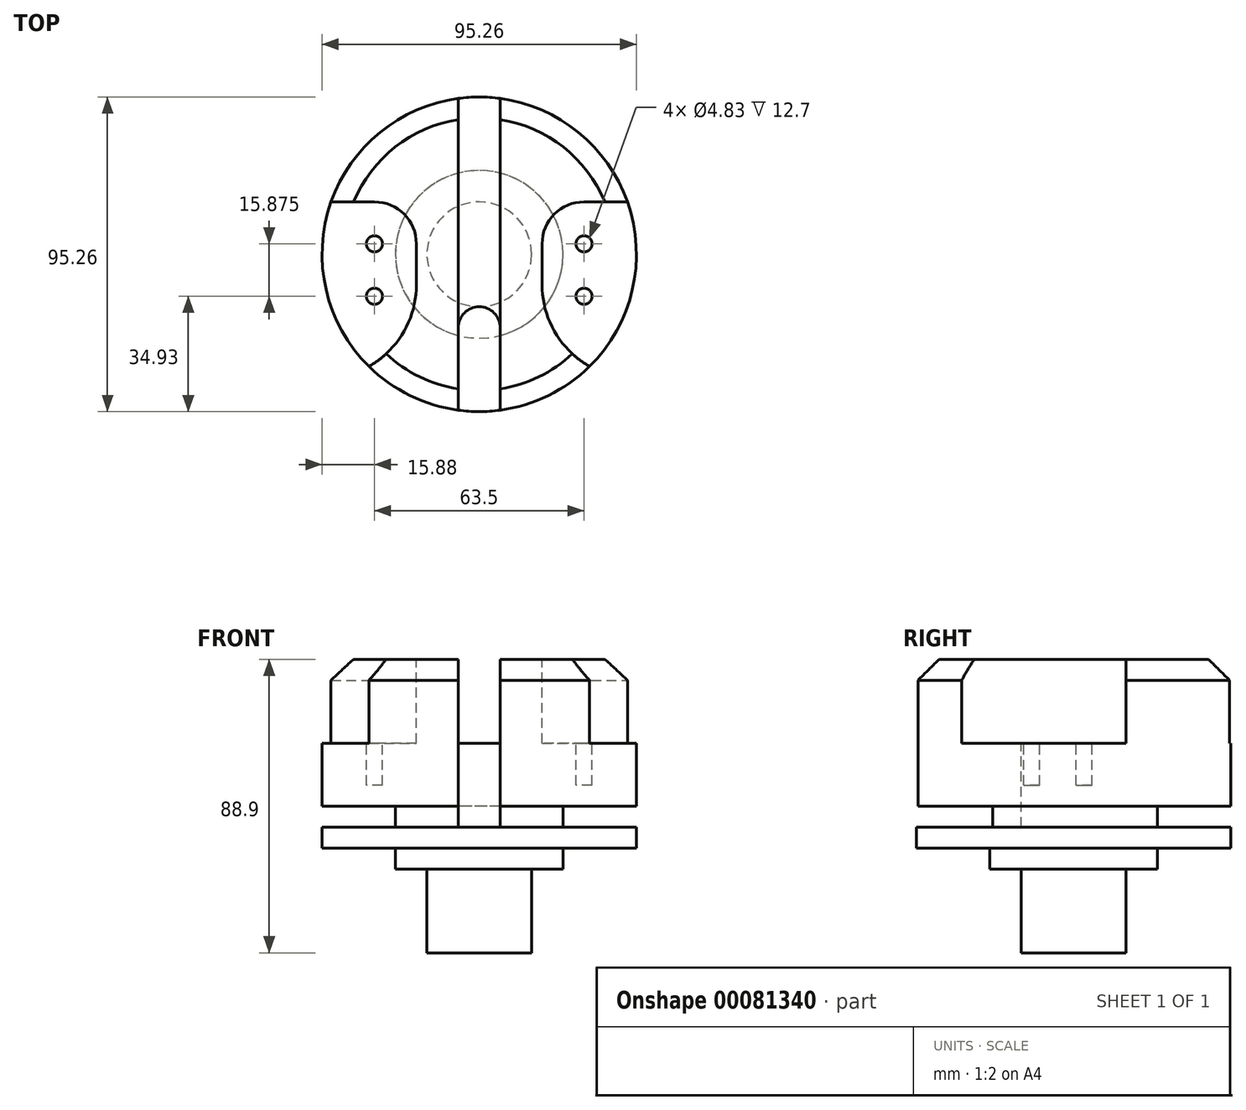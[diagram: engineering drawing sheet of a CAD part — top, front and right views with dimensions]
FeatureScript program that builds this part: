
annotation { "Feature Type Name" : "Feature", "Feature Type Description" : "" }
export const myFeature = defineFeature(function(context is Context, id is Id, definition is map)
    precondition{}
    {
        {
            var Q0;
            Q0=qCreatedBy(makeId("Front.planeOp"),FACE);
            var sketch = newSketch(context, id + "F0", { "sketchPlane" : qUnion([Q0])});
            skLineSegment(sketch, "E0", {"start": v(15.87, 0) * mm, "end": v(15.87, 25.4) * mm});
            skLineSegment(sketch, "E1", {"start": v(15.87, 25.4) * mm, "end": v(25.4, 25.4) * mm});
            skLineSegment(sketch, "E2", {"start": v(25.4, 25.4) * mm, "end": v(25.4, 31.75) * mm});
            skLineSegment(sketch, "E3", {"start": v(47.63, 31.75) * mm, "end": v(25.4, 31.75) * mm});
            skLineSegment(sketch, "E4", {"start": v(47.63, 31.75) * mm, "end": v(47.63, 38.1) * mm});
            skLineSegment(sketch, "E5", {"start": v(25.4, 38.1) * mm, "end": v(47.63, 38.1) * mm});
            skLineSegment(sketch, "E6", {"start": v(25.4, 38.1) * mm, "end": v(25.4, 44.45) * mm});
            skLineSegment(sketch, "E7", {"start": v(28.9, 44.45) * mm, "end": v(25.4, 44.45) * mm});
            skLineSegment(sketch, "E8", {"start": v(28.9, 44.45) * mm, "end": v(47.63, 44.45) * mm});
            skLineSegment(sketch, "E9", {"start": v(47.63, 44.45) * mm, "end": v(47.63, 88.9) * mm});
            skLineSegment(sketch, "E10", {"start": v(47.63, 88.9) * mm, "end": v(0, 88.9) * mm});
            skLineSegment(sketch, "E11", {"start": v(0, 88.9) * mm, "end": v(0, 0) * mm});
            skLineSegment(sketch, "E12", {"start": v(0, 0) * mm, "end": v(15.87, 0) * mm});
            skSolve(sketch);
        }
        {
            var Q0;
            Q0=makeQuery(id+"F0.imprint","IMPRINT",FACE,{"disambiguationData":[TD([[makeQuery(id+"F0.imprint","IMPRINT",EDGE,{"derivedFrom":sQuery(id+"F0.wireOp",EDGE,"E0")}),1.0]])]});
            var Q1;
            Q1=sQuery(id+"F0.wireOp",EDGE,"E11");
            revolve(context, id + "F1", {"surfaceOperationType" : NewSurfaceOperationType.NEW, "entities" : qUnion([Q0]), "axis" : qUnion([Q1]), "revolveType" : RevolveType.FULL});
        }
        {
            var Q0;
            Q0=makeQuery(id+"F1.opRevolve","SWEPT_FACE",FACE,{"disambiguationData":[OSD([sQuery(id+"F0.wireOp",EDGE,"E10")])]});
            var sketch = newSketch(context, id + "F2", { "sketchPlane" : qUnion([Q0])});
            skLineSegment(sketch, "E13", {"start": v(-19.05, -55.7) * mm, "end": v(-19.05, 3.17) * mm});
            skLineSegment(sketch, "E14", {"start": v(-31.75, 15.87) * mm, "end": v(-57.15, 15.87) * mm});
            skLineSegment(sketch, "E15", {"start": v(19.05, -52.05) * mm, "end": v(19.05, 3.18) * mm});
            skLineSegment(sketch, "E16", {"start": v(31.75, 15.88) * mm, "end": v(57.15, 15.88) * mm});
            skLineSegment(sketch, "E17", {"start": v(-6.35, 54.02) * mm, "end": v(-6.35, -53.72) * mm});
            skLineSegment(sketch, "E18", {"start": v(-6.35, -53.72) * mm, "end": v(6.35, -53.72) * mm});
            skLineSegment(sketch, "E19", {"start": v(6.35, -53.72) * mm, "end": v(6.35, 54.02) * mm});
            skLineSegment(sketch, "E20", {"start": v(6.35, 54.02) * mm, "end": v(-6.35, 54.02) * mm});
            skLineSegment(sketch, "E21", {"start": v(0, 0) * mm, "end": v(0, -53.72) * mm, "construction": true});
            skPoint(sketch, "E22.visualSharp", {"position": v(19.05, 15.88) * mm});
            skArc(sketch, "E22.filletArc", {"start": v(31.75, 15.88) * mm, "mid": v(22.77, 12.16) * mm, "end": v(19.05, 3.18) * mm});
            skPoint(sketch, "E23.visualSharp", {"position": v(-19.05, 15.87) * mm});
            skArc(sketch, "E23.filletArc", {"start": v(-19.05, 3.17) * mm, "mid": v(-22.77, 12.16) * mm, "end": v(-31.75, 15.88) * mm});
            skLineSegment(sketch, "E24", {"start": v(0, 0) * mm, "end": v(76.66, -44.26) * mm, "construction": true});
            skLineSegment(sketch, "E25.0", {"start": v(-4.76, -8.25) * mm, "end": v(71.9, -52.5) * mm, "construction": true});
            skLineSegment(sketch, "E26.0", {"start": v(-6.35, -11) * mm, "end": v(70.3, -55.26) * mm});
            skArc(sketch, "E27", {"start": v(19.05, -9.17) * mm, "mid": v(22.88, -23.45) * mm, "end": v(33.34, -33.91) * mm});
            skLineSegment(sketch, "E28.MirrorCS", {"start": v(6.35, -11) * mm, "end": v(-70.3, -55.26) * mm});
            skArc(sketch, "E29.MirrorCS", {"start": v(-19.05, -9.17) * mm, "mid": v(-22.88, -23.45) * mm, "end": v(-33.34, -33.91) * mm});
            skCircle(sketch, "E30", {"center": v(31.75, 3.17) * mm, "radius": 2.41 * mm});
            skCircle(sketch, "E31", {"center": v(31.75, -12.7) * mm, "radius": 2.41 * mm});
            skCircle(sketch, "E32", {"center": v(-31.75, 3.17) * mm, "radius": 2.41 * mm});
            skCircle(sketch, "E33", {"center": v(-31.75, -12.7) * mm, "radius": 2.41 * mm});
            skLineSegment(sketch, "E34", {"start": v(-6.35, -22.23) * mm, "end": v(6.35, -22.22) * mm});
            skArc(sketch, "E35", {"start": v(6.35, -22.22) * mm, "mid": v(0, -15.87) * mm, "end": v(-6.35, -22.22) * mm});
            skSolve(sketch);
        }
        {
            var Q0;
            {var subQ0=sQuery(id+"F2.wireOp",EDGE,"E22.filletArc");Q0=makeQuery(id+"F2.imprint","IMPRINT",FACE,{"disambiguationData":[TD([[makeQuery(id+"F2.imprint","IMPRINT",EDGE,{"derivedFrom":subQ0}),1.0]])]});}
            var Q1;
            {var subQ0=sQuery(id+"F2.wireOp",EDGE,"E17");var subQ1=makeQuery(id+"F1.opRevolve","SWEPT_EDGE",EDGE,{"disambiguationData":[OSD([sQuery(id+"F0.wireOp",EDGE,"E9"),sQuery(id+"F0.wireOp",EDGE,"E10")])]});var subQ2=makeQuery(id+"F2.imprint","INTERSECT",VERTEX,{"disambiguationData":[OD(0.0)],"derivedFrom":[subQ1,subQ0]});Q1=makeQuery(id+"F2.imprint","IMPRINT",FACE,{"disambiguationData":[TD([[makeQuery(id+"F2.imprint","IMPRINT",EDGE,{"disambiguationData":[TD([[subQ2,-1.0]])],"derivedFrom":subQ0}),1.0]])]});}
            var Q2;
            {var subQ0=sQuery(id+"F2.wireOp",EDGE,"E23.filletArc");Q2=makeQuery(id+"F2.imprint","IMPRINT",FACE,{"disambiguationData":[TD([[makeQuery(id+"F2.imprint","IMPRINT",EDGE,{"derivedFrom":subQ0}),1.0]])]});}
            var Q3;
            {var subQ3=sQuery(id+"F2.wireOp",EDGE,"E26.0");var subQ5=sQuery(id+"F2.wireOp",EDGE,"E19");var subQ6=makeQuery(id+"F2.imprint","INTERSECT",VERTEX,{"derivedFrom":[subQ5,subQ3]});Q3=makeQuery(id+"F2.imprint","IMPRINT",FACE,{"disambiguationData":[TD([[makeQuery(id+"F2.imprint","IMPRINT",EDGE,{"disambiguationData":[TD([[subQ6,1.0]])],"derivedFrom":subQ3}),-1.0]])]});}
            var Q4;
            {var subQ0=sQuery(id+"F2.wireOp",EDGE,"E28.MirrorCS");var subQ1=sQuery(id+"F2.wireOp",EDGE,"E19");var subQ2=makeQuery(id+"F2.imprint","INTERSECT",VERTEX,{"derivedFrom":[subQ1,subQ0]});Q4=makeQuery(id+"F2.imprint","IMPRINT",FACE,{"disambiguationData":[TD([[makeQuery(id+"F2.imprint","IMPRINT",EDGE,{"disambiguationData":[TD([[subQ2,1.0]])],"derivedFrom":subQ1}),1.0]])]});}
            var Q5;
            {var subQ0=sQuery(id+"F2.wireOp",EDGE,"E26.0");var subQ1=sQuery(id+"F2.wireOp",EDGE,"E17");var subQ2=makeQuery(id+"F2.imprint","INTERSECT",VERTEX,{"derivedFrom":[subQ1,subQ0]});Q5=makeQuery(id+"F2.imprint","IMPRINT",FACE,{"disambiguationData":[TD([[makeQuery(id+"F2.imprint","IMPRINT",EDGE,{"disambiguationData":[TD([[subQ2,-1.0]])],"derivedFrom":subQ1}),1.0]])]});}
            var Q6;
            Q6=makeQuery(id+"F2.imprint","IMPRINT",FACE,{"disambiguationData":[TD([[makeQuery(id+"F2.imprint","IMPRINT",EDGE,{"derivedFrom":sQuery(id+"F2.wireOp",EDGE,"E32")}),1.0]])]});
            var Q7;
            Q7=makeQuery(id+"F2.imprint","IMPRINT",FACE,{"disambiguationData":[TD([[makeQuery(id+"F2.imprint","IMPRINT",EDGE,{"derivedFrom":sQuery(id+"F2.wireOp",EDGE,"E33")}),1.0]])]});
            var Q8;
            Q8=makeQuery(id+"F2.imprint","IMPRINT",FACE,{"disambiguationData":[TD([[makeQuery(id+"F2.imprint","IMPRINT",EDGE,{"derivedFrom":sQuery(id+"F2.wireOp",EDGE,"E31")}),1.0]])]});
            var Q9;
            Q9=makeQuery(id+"F2.imprint","IMPRINT",FACE,{"disambiguationData":[TD([[makeQuery(id+"F2.imprint","IMPRINT",EDGE,{"derivedFrom":sQuery(id+"F2.wireOp",EDGE,"E30")}),1.0]])]});
            extrude(context, id + "F3", {"entities" : qUnion([Q0, Q1, Q2, Q3, Q4, Q5, Q6, Q7, Q8, Q9]), "operationType" : NewBodyOperationType.REMOVE, "oppositeDirection" : true, "depth" : 25.4 * mm, "offsetDistance" : 25.4 * mm});
        }
        {
            var Q0;
            Q0=makeQuery(id+"F2.imprint","IMPRINT",FACE,{"disambiguationData":[TD([[makeQuery(id+"F2.imprint","IMPRINT",EDGE,{"derivedFrom":sQuery(id+"F2.wireOp",EDGE,"E34")}),1.0]])]});
            var Q1;
            {var subQ1=sQuery(id+"F2.wireOp",EDGE,"E34");Q1=makeQuery(id+"F2.imprint","IMPRINT",FACE,{"disambiguationData":[TD([[makeQuery(id+"F2.imprint","IMPRINT",EDGE,{"derivedFrom":subQ1}),-1.0]])]});}
            extrude(context, id + "F4", {"entities" : qUnion([Q0, Q1]), "operationType" : NewBodyOperationType.REMOVE, "oppositeDirection" : true, "depth" : 50.8 * mm, "offsetDistance" : 25.4 * mm});
        }
        {
            var Q0;
            Q0=makeQuery(id+"F2.imprint","IMPRINT",FACE,{"disambiguationData":[TD([[makeQuery(id+"F2.imprint","IMPRINT",EDGE,{"derivedFrom":sQuery(id+"F2.wireOp",EDGE,"E32")}),1.0]])]});
            var Q1;
            Q1=makeQuery(id+"F2.imprint","IMPRINT",FACE,{"disambiguationData":[TD([[makeQuery(id+"F2.imprint","IMPRINT",EDGE,{"derivedFrom":sQuery(id+"F2.wireOp",EDGE,"E33")}),1.0]])]});
            var Q2;
            Q2=makeQuery(id+"F2.imprint","IMPRINT",FACE,{"disambiguationData":[TD([[makeQuery(id+"F2.imprint","IMPRINT",EDGE,{"derivedFrom":sQuery(id+"F2.wireOp",EDGE,"E30")}),1.0]])]});
            var Q3;
            Q3=makeQuery(id+"F2.imprint","IMPRINT",FACE,{"disambiguationData":[TD([[makeQuery(id+"F2.imprint","IMPRINT",EDGE,{"derivedFrom":sQuery(id+"F2.wireOp",EDGE,"E31")}),1.0]])]});
            extrude(context, id + "F5", {"entities" : qUnion([Q0, Q1, Q2, Q3]), "operationType" : NewBodyOperationType.REMOVE, "oppositeDirection" : true, "depth" : 38.1 * mm, "offsetDistance" : 25.4 * mm});
        }
        {
            var Q0;
            Q0=makeQuery(id+"F1.opRevolve","SWEPT_FACE",FACE,{"disambiguationData":[OSD([sQuery(id+"F0.wireOp",EDGE,"E7"),sQuery(id+"F0.wireOp",EDGE,"E8")])]});
            var sketch = newSketch(context, id + "F6", { "sketchPlane" : qUnion([Q0])});
            skLineSegment(sketch, "E36", {"start": v(0, 0) * mm, "end": v(-18.74, 43.78) * mm});
            skSolve(sketch);
        }
        {
            var Q0;
            Q0=makeQuery(id+"F3.boolean.opBoolean","COPY",VERTEX,{"derivedFrom":makeQuery(id+"F3.opExtrude","CAP_VERTEX",VERTEX,{"disambiguationData":[OSD([sQuery(id+"F0.wireOp",EDGE,"E9"),sQuery(id+"F0.wireOp",EDGE,"E10"),sQuery(id+"F2.wireOp",EDGE,"E28.MirrorCS")])],"isStart":false})});
            var Q1;
            Q1=sQuery(id+"F6.wireOp",VERTEX,"E36.end");
            var Q2;
            Q2=makeQuery(id+"F4.boolean.opBoolean","INTERSECT",VERTEX,{"derivedFrom":[makeQuery(id+"F1.opRevolve","SWEPT_FACE",FACE,{"disambiguationData":[OSD([sQuery(id+"F0.wireOp",EDGE,"E6")])]}),makeQuery(id+"F4.opExtrude","SWEPT_FACE",FACE,{"disambiguationData":[OSD([sQuery(id+"F2.wireOp",EDGE,"E17")])]})]});
            cPlane(context, id + "F7", {"entities" : qUnion([Q0, Q1, Q2]), "cplaneType" : CPlaneType.THREE_POINT, "offset" : 25.4 * mm, "width" : 152.4 * mm, "height" : 152.4 * mm});
        }
        {
            var Q0;
            {var subQ0=makeQuery(id+"F3.opExtrude","SWEPT_FACE",FACE,{"disambiguationData":[OSD([sQuery(id+"F2.wireOp",EDGE,"E26.0")])]});var subQ1=sQuery(id+"F2.wireOp",EDGE,"E19");var subQ2=sQuery(id+"F0.wireOp",EDGE,"E10");var subQ4=sQuery(id+"F0.wireOp",EDGE,"E9");Q0=makeQuery(id+"F4.boolean.opBoolean","SPLIT",EDGE,{"disambiguationData":[TD([makeQuery(id+"F3.boolean.opBoolean","COPY",FACE,{"derivedFrom":makeQuery(id+"F3.opExtrude","SWEPT_FACE",FACE,{"disambiguationData":[OSD([subQ1])]})})])],"derivedFrom":makeQuery(id+"F3.boolean.opBoolean","SPLIT",EDGE,{"disambiguationData":[TD([subQ0])],"derivedFrom":makeQuery(id+"F1.opRevolve","SWEPT_EDGE",EDGE,{"disambiguationData":[OSD([subQ4,subQ2])]})})});}
            var Q1;
            {var subQ1=sQuery(id+"F2.wireOp",EDGE,"E17");var subQ2=sQuery(id+"F0.wireOp",EDGE,"E10");var subQ4=sQuery(id+"F0.wireOp",EDGE,"E9");Q1=makeQuery(id+"F4.boolean.opBoolean","SPLIT",EDGE,{"disambiguationData":[TD([makeQuery(id+"F3.boolean.opBoolean","COPY",FACE,{"derivedFrom":makeQuery(id+"F3.opExtrude","SWEPT_FACE",FACE,{"disambiguationData":[OSD([subQ1])]})})])],"derivedFrom":makeQuery(id+"F3.boolean.opBoolean","SPLIT",EDGE,{"disambiguationData":[TD([makeQuery(id+"F3.opExtrude","SWEPT_FACE",FACE,{"disambiguationData":[OSD([sQuery(id+"F2.wireOp",EDGE,"E26.0")])]})])],"derivedFrom":makeQuery(id+"F1.opRevolve","SWEPT_EDGE",EDGE,{"disambiguationData":[OSD([subQ4,subQ2])]})})});}
            var Q2;
            {var subQ0=sQuery(id+"F0.wireOp",EDGE,"E9");var subQ1=sQuery(id+"F0.wireOp",EDGE,"E10");Q2=makeQuery(id+"F3.boolean.opBoolean","SPLIT",EDGE,{"disambiguationData":[TD([makeQuery(id+"F3.opExtrude","SWEPT_FACE",FACE,{"disambiguationData":[OSD([sQuery(id+"F2.wireOp",EDGE,"E14")])]})])],"derivedFrom":makeQuery(id+"F1.opRevolve","SWEPT_EDGE",EDGE,{"disambiguationData":[OSD([subQ0,subQ1])]})});}
            var Q3;
            {var subQ0=sQuery(id+"F0.wireOp",EDGE,"E9");var subQ1=sQuery(id+"F0.wireOp",EDGE,"E10");Q3=makeQuery(id+"F3.boolean.opBoolean","SPLIT",EDGE,{"disambiguationData":[TD([makeQuery(id+"F3.opExtrude","SWEPT_FACE",FACE,{"disambiguationData":[OSD([sQuery(id+"F2.wireOp",EDGE,"E16")])]})])],"derivedFrom":makeQuery(id+"F1.opRevolve","SWEPT_EDGE",EDGE,{"disambiguationData":[OSD([subQ0,subQ1])]})});}
            chamfer(context, id + "F8", {"entities" : qUnion([Q0, Q1, Q2, Q3]), "width" : 6.35 * mm, "tangentPropagation" : true});
        }
    });
